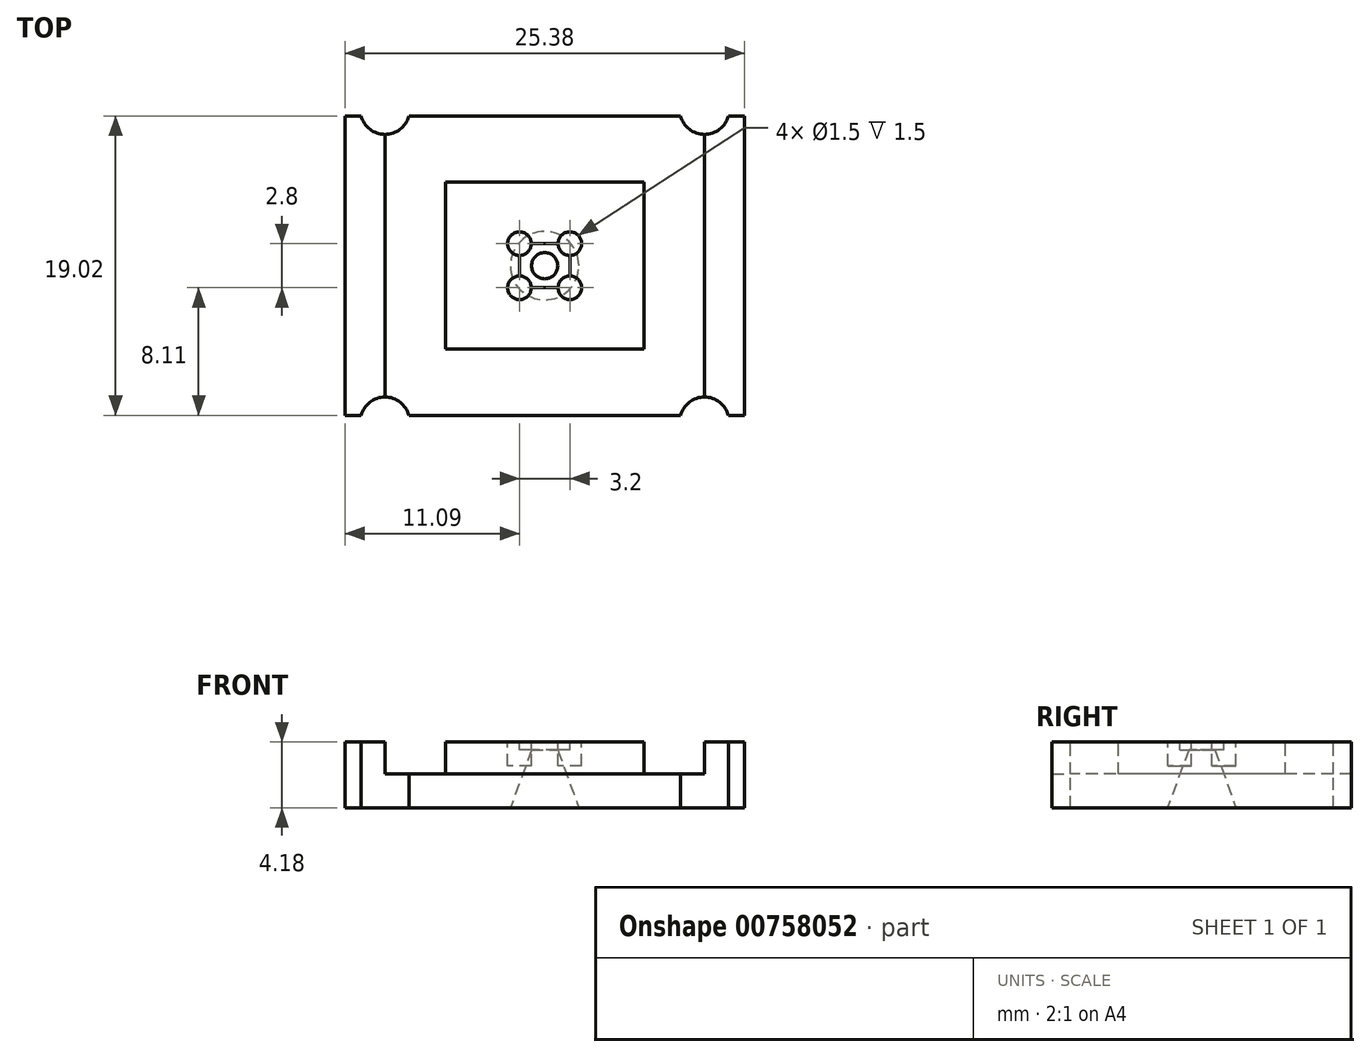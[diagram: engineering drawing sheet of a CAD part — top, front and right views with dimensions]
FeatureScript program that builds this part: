
annotation { "Feature Type Name" : "Feature", "Feature Type Description" : "" }
export const myFeature = defineFeature(function(context is Context, id is Id, definition is map)
    precondition{}
    {
        {
            assignVariable(context, id + "F0", {"name" : "CutDepth", "anyValue" : 0.5});
        }
        {
            var Q0;
            Q0=qCreatedBy(makeId("Top.planeOp"),FACE);
            var sketch = newSketch(context, id + "F1", { "sketchPlane" : qUnion([Q0])});
            skLineSegment(sketch, "E0.bottom", {"start": v(12.69, 9.51) * mm, "end": v(-12.69, 9.51) * mm});
            skLineSegment(sketch, "E0.top", {"start": v(12.69, -9.51) * mm, "end": v(-12.68, -9.51) * mm});
            skLineSegment(sketch, "E0.left", {"start": v(12.69, 9.51) * mm, "end": v(12.69, -9.51) * mm});
            skLineSegment(sketch, "E0.right", {"start": v(-12.69, 9.51) * mm, "end": v(-12.69, -9.51) * mm});
            skPoint(sketch, "E0.middle", {"position": v(0, 0) * mm});
            skSolve(sketch);
        }
        {
            var Q0;
            Q0 = qSketchRegion(id + "F1", true);
            extrude(context, id + "F2", {"entities" : qUnion([Q0]), "depth" : 4.18 * mm, "offsetDistance" : 25 * mm});
        }
        {
            var Q0;
            Q0=makeQuery(id+"F2.opExtrude","CAP_FACE",FACE,{"disambiguationData":[OSD([sQuery(id+"F1.wireOp",EDGE,"E0.bottom"),sQuery(id+"F1.wireOp",EDGE,"E0.top"),sQuery(id+"F1.wireOp",EDGE,"E0.left"),sQuery(id+"F1.wireOp",EDGE,"E0.right")])],"isStart":false});
            var sketch = newSketch(context, id + "F3", { "sketchPlane" : qUnion([Q0])});
            skLineSegment(sketch, "E1.bottom", {"start": v(10.15, 9.51) * mm, "end": v(-10.15, 9.51) * mm});
            skLineSegment(sketch, "E1.top", {"start": v(10.15, -9.5) * mm, "end": v(-10.15, -9.51) * mm});
            skLineSegment(sketch, "E1.left", {"start": v(10.15, 9.51) * mm, "end": v(10.15, -9.5) * mm});
            skLineSegment(sketch, "E1.right", {"start": v(-10.15, 9.51) * mm, "end": v(-10.14, -9.51) * mm});
            skPoint(sketch, "E1.middle", {"position": v(0, 0) * mm});
            skLineSegment(sketch, "E2.bottom", {"start": v(6.3, 5.3) * mm, "end": v(-6.3, 5.3) * mm});
            skLineSegment(sketch, "E2.top", {"start": v(6.3, -5.3) * mm, "end": v(-6.3, -5.3) * mm});
            skLineSegment(sketch, "E2.left", {"start": v(6.3, 5.3) * mm, "end": v(6.3, -5.3) * mm});
            skLineSegment(sketch, "E2.right", {"start": v(-6.3, 5.3) * mm, "end": v(-6.3, -5.3) * mm});
            skSolve(sketch);
        }
        {
            var Q0;
            Q0=makeQuery(id+"F3.imprint","IMPRINT",FACE,{"disambiguationData":[TD([[makeQuery(id+"F3.imprint","IMPRINT",EDGE,{"derivedFrom":sQuery(id+"F3.wireOp",EDGE,"E1.bottom")}),1.0]])]});
            extrude(context, id + "F4", {"entities" : qUnion([Q0]), "operationType" : NewBodyOperationType.REMOVE, "oppositeDirection" : true, "depth" : 2.03 * mm, "offsetDistance" : 25 * mm});
        }
        {
            var Q0;
            Q0=makeQuery(id+"F4.boolean.opBoolean","SPLIT",FACE,{"disambiguationData":[TD([makeQuery(id+"F4.opExtrude","SWEPT_FACE",FACE,{"disambiguationData":[OSD([sQuery(id+"F3.wireOp",EDGE,"E2.bottom")])]})])],"derivedFrom":makeQuery(id+"F2.opExtrude","CAP_FACE",FACE,{"disambiguationData":[OSD([sQuery(id+"F1.wireOp",EDGE,"E0.bottom"),sQuery(id+"F1.wireOp",EDGE,"E0.top"),sQuery(id+"F1.wireOp",EDGE,"E0.left"),sQuery(id+"F1.wireOp",EDGE,"E0.right")])],"isStart":false})});
            var sketch = newSketch(context, id + "F5", { "sketchPlane" : qUnion([Q0])});
            skCircle(sketch, "E3", {"center": v(-10.15, 9.9) * mm, "radius": 1.57 * mm});
            skLineSegment(sketch, "E4.0.0", {"start": v(-10.14, -9.51) * mm, "end": v(-10.15, 9.51) * mm, "construction": true});
            skLineSegment(sketch, "E5", {"start": v(0, 0) * mm, "end": v(0, 2.24) * mm, "construction": true});
            skLineSegment(sketch, "E6", {"start": v(0, 0) * mm, "end": v(-2.16, 0) * mm, "construction": true});
            skCircle(sketch, "E7.MirrorC", {"center": v(10.15, 9.9) * mm, "radius": 1.57 * mm});
            skCircle(sketch, "E8.MirrorC", {"center": v(-10.15, -9.9) * mm, "radius": 1.57 * mm});
            skCircle(sketch, "E9.MirrorC", {"center": v(10.15, -9.9) * mm, "radius": 1.57 * mm});
            skSolve(sketch);
        }
        {
            var Q0;
            Q0 = qSketchRegion(id + "F5", true);
            extrude(context, id + "F6", {"entities" : qUnion([Q0]), "operationType" : NewBodyOperationType.REMOVE, "endBound" : BoundingType.THROUGH_ALL, "oppositeDirection" : true, "depth" : 25 * mm, "offsetDistance" : 25 * mm});
        }
        {
            var Q0;
            Q0=makeQuery(id+"F4.boolean.opBoolean","SPLIT",FACE,{"disambiguationData":[TD([makeQuery(id+"F4.opExtrude","SWEPT_FACE",FACE,{"disambiguationData":[OSD([sQuery(id+"F3.wireOp",EDGE,"E2.bottom")])]})])],"derivedFrom":makeQuery(id+"F2.opExtrude","CAP_FACE",FACE,{"disambiguationData":[OSD([sQuery(id+"F1.wireOp",EDGE,"E0.bottom"),sQuery(id+"F1.wireOp",EDGE,"E0.top"),sQuery(id+"F1.wireOp",EDGE,"E0.left"),sQuery(id+"F1.wireOp",EDGE,"E0.right")])],"isStart":false})});
            var sketch = newSketch(context, id + "F7", { "sketchPlane" : qUnion([Q0])});
            skLineSegment(sketch, "E10.bottom", {"start": v(-1.6, 1.4) * mm, "end": v(1.6, 1.4) * mm});
            skLineSegment(sketch, "E10.top", {"start": v(-1.6, -1.4) * mm, "end": v(1.6, -1.4) * mm});
            skLineSegment(sketch, "E10.left", {"start": v(-1.6, 1.4) * mm, "end": v(-1.6, -1.4) * mm});
            skLineSegment(sketch, "E10.right", {"start": v(1.6, 1.4) * mm, "end": v(1.6, -1.4) * mm});
            skPoint(sketch, "E10.middle", {"position": v(0, 0) * mm});
            skSolve(sketch);
        }
        {
            var Q0;
            Q0 = qSketchRegion(id + "F7", true);
            extrude(context, id + "F8", {"entities" : qUnion([Q0]), "operationType" : NewBodyOperationType.REMOVE, "flatOperationType" : FlatOperationType.REMOVE, "oppositeDirection" : true, "depth" : (getVariable(context, 'CutDepth')) * mm, "offsetDistance" : 25 * mm, "domain" : OperationDomain.MODEL});
        }
        {
            var Q0;
            Q0=makeQuery(id+"F4.boolean.opBoolean","SPLIT",FACE,{"disambiguationData":[TD([makeQuery(id+"F4.opExtrude","SWEPT_FACE",FACE,{"disambiguationData":[OSD([sQuery(id+"F3.wireOp",EDGE,"E2.bottom")])]})])],"derivedFrom":makeQuery(id+"F2.opExtrude","CAP_FACE",FACE,{"disambiguationData":[OSD([sQuery(id+"F1.wireOp",EDGE,"E0.bottom"),sQuery(id+"F1.wireOp",EDGE,"E0.top"),sQuery(id+"F1.wireOp",EDGE,"E0.left"),sQuery(id+"F1.wireOp",EDGE,"E0.right")])],"isStart":false})});
            var sketch = newSketch(context, id + "F9", { "sketchPlane" : qUnion([Q0])});
            skCircle(sketch, "E11", {"center": v(-1.6, 1.4) * mm, "radius": 0.75 * mm});
            skCircle(sketch, "E12", {"center": v(1.6, 1.4) * mm, "radius": 0.75 * mm});
            skCircle(sketch, "E13", {"center": v(1.6, -1.4) * mm, "radius": 0.75 * mm});
            skCircle(sketch, "E14", {"center": v(-1.6, -1.4) * mm, "radius": 0.75 * mm});
            skSolve(sketch);
        }
        {
            var Q0;
            Q0 = qSketchRegion(id + "F9", true);
            extrude(context, id + "F10", {"entities" : qUnion([Q0]), "operationType" : NewBodyOperationType.REMOVE, "oppositeDirection" : true, "depth" : 1.5 * mm, "offsetDistance" : 25 * mm});
        }
        {
            var Q0;
            Q0=makeQuery(id+"F8.boolean.opBoolean","COPY",FACE,{"derivedFrom":makeQuery(id+"F8.opExtrude","CAP_FACE",FACE,{"disambiguationData":[OSD([sQuery(id+"F7.wireOp",EDGE,"E10.bottom"),sQuery(id+"F7.wireOp",EDGE,"E10.top"),sQuery(id+"F7.wireOp",EDGE,"E10.left"),sQuery(id+"F7.wireOp",EDGE,"E10.right")])],"isStart":false})});
            var sketch = newSketch(context, id + "F11", { "sketchPlane" : qUnion([Q0])});
            skCircle(sketch, "E15", {"center": v(0, 0) * mm, "radius": 0.84 * mm});
            skSolve(sketch);
        }
        {
            var Q0;
            Q0 = qSketchRegion(id + "F11", true);
            extrude(context, id + "F12", {"entities" : qUnion([Q0]), "operationType" : NewBodyOperationType.REMOVE, "endBound" : BoundingType.THROUGH_ALL, "oppositeDirection" : true, "depth" : 25 * mm, "offsetDistance" : 25 * mm, "hasDraft" : true, "draftAngle" : 20 * degree});
        }
    });
